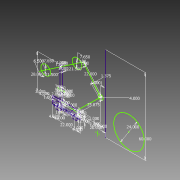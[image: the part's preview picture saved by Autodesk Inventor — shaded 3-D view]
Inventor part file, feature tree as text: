
AUTODESK INVENTOR PART (.ipt)
format: ipt  version: 2014 (Build 180170000, 170)  size: 140,800 bytes
history: native  units: in
note: dims shown in document units (in); Inventor stores cm internally (conversion verified against a paired STEP export)
features: sketch x1
ambient origin geometry x8: Origin, YZ Plane, XZ Plane, XY Plane, X Axis, Y Axis, Z Axis, Center Point
feature tree (1):
  sketch  "Sketch1"  dims[d0=22.0in d1=2.0in d2=6.0in d3=6.0in d4=4.5in d5=4.5in d6=1.0in d7=1.0in d8=1.0in d9=3.0in d10=1.5in d11=3.0in d12=1.0in d13=2.0in d14=28.0in d15=1.0in d16=14.0in d24=0.0in d26=2.0in d29=0.25in d36=0.5in d37=2.5in d44=0.5in d45=1.0in d46=1.0in d48=21.5in d49=21.5in d50=7.65in d51=7.65in d52=6.5in d53=6.5in d56=25.875in d57=4.0in d68=60.0in d70=1.375in d72=0.0in d74=0.5in d75=0.0in d108=2.0in d109=1.0in d110=0.0in d117=0.5in d119=15.0in d120=0.5in d121=1.0in d122=20.0in d125=0.5in d126=0.5in d127=0.5in d146=22.0in d154=24.0in d167=5.0in d168=1.0in d169=0.5in d170=0.5in d171=0.5in]
